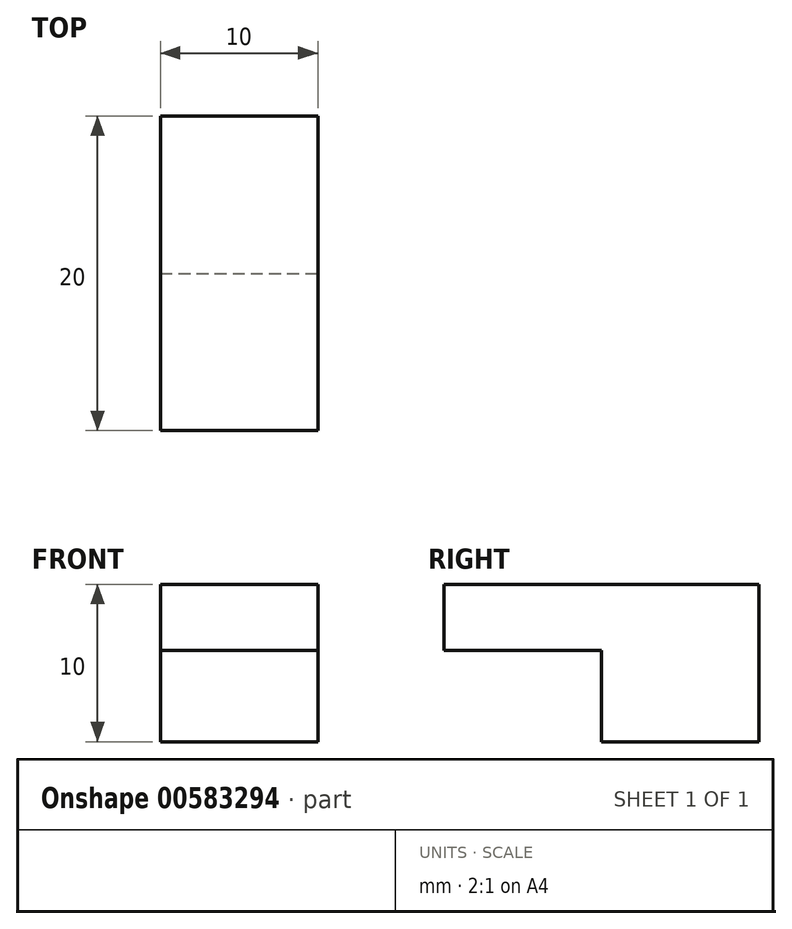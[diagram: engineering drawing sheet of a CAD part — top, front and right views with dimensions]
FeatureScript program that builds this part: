
annotation { "Feature Type Name" : "Feature", "Feature Type Description" : "" }
export const myFeature = defineFeature(function(context is Context, id is Id, definition is map)
    precondition{}
    {
        {
            var Q0;
            Q0=qCreatedBy(makeId("Top.planeOp"),FACE);
            var sketch = newSketch(context, id + "F0", { "sketchPlane" : qUnion([Q0])});
            skLineSegment(sketch, "E0.bottom", {"start": v(5, 5) * mm, "end": v(-5, 5) * mm});
            skLineSegment(sketch, "E0.top", {"start": v(5, -5) * mm, "end": v(-5, -5) * mm});
            skLineSegment(sketch, "E0.left", {"start": v(5, 5) * mm, "end": v(5, -5) * mm});
            skLineSegment(sketch, "E0.right", {"start": v(-5, 5) * mm, "end": v(-5, -5) * mm});
            skPoint(sketch, "E0.middle", {"position": v(0, 0) * mm});
            skSolve(sketch);
        }
        {
            var Q0;
            Q0 = qSketchRegion(id + "F0", true);
            extrude(context, id + "F1", {"entities" : qUnion([Q0]), "depth" : 10 * mm, "offsetDistance" : 25 * mm});
        }
        {
            var Q0;
            Q0=makeQuery(id+"F1.opExtrude","SWEPT_FACE",FACE,{"disambiguationData":[OSD([sQuery(id+"F0.wireOp",EDGE,"E0.top")])]});
            var sketch = newSketch(context, id + "F2", { "sketchPlane" : qUnion([Q0])});
            skLineSegment(sketch, "E1.bottom", {"start": v(-5, 10) * mm, "end": v(5, 10) * mm});
            skLineSegment(sketch, "E1.top", {"start": v(-5, 5.8) * mm, "end": v(5, 5.8) * mm});
            skLineSegment(sketch, "E1.left", {"start": v(-5, 10) * mm, "end": v(-5, 5.8) * mm});
            skLineSegment(sketch, "E1.right", {"start": v(5, 10) * mm, "end": v(5, 5.8) * mm});
            skSolve(sketch);
        }
        {
            var Q0;
            Q0 = qSketchRegion(id + "F2", true);
            extrude(context, id + "F3", {"entities" : qUnion([Q0]), "operationType" : NewBodyOperationType.ADD, "depth" : 10 * mm, "offsetDistance" : 25 * mm});
        }
    });
